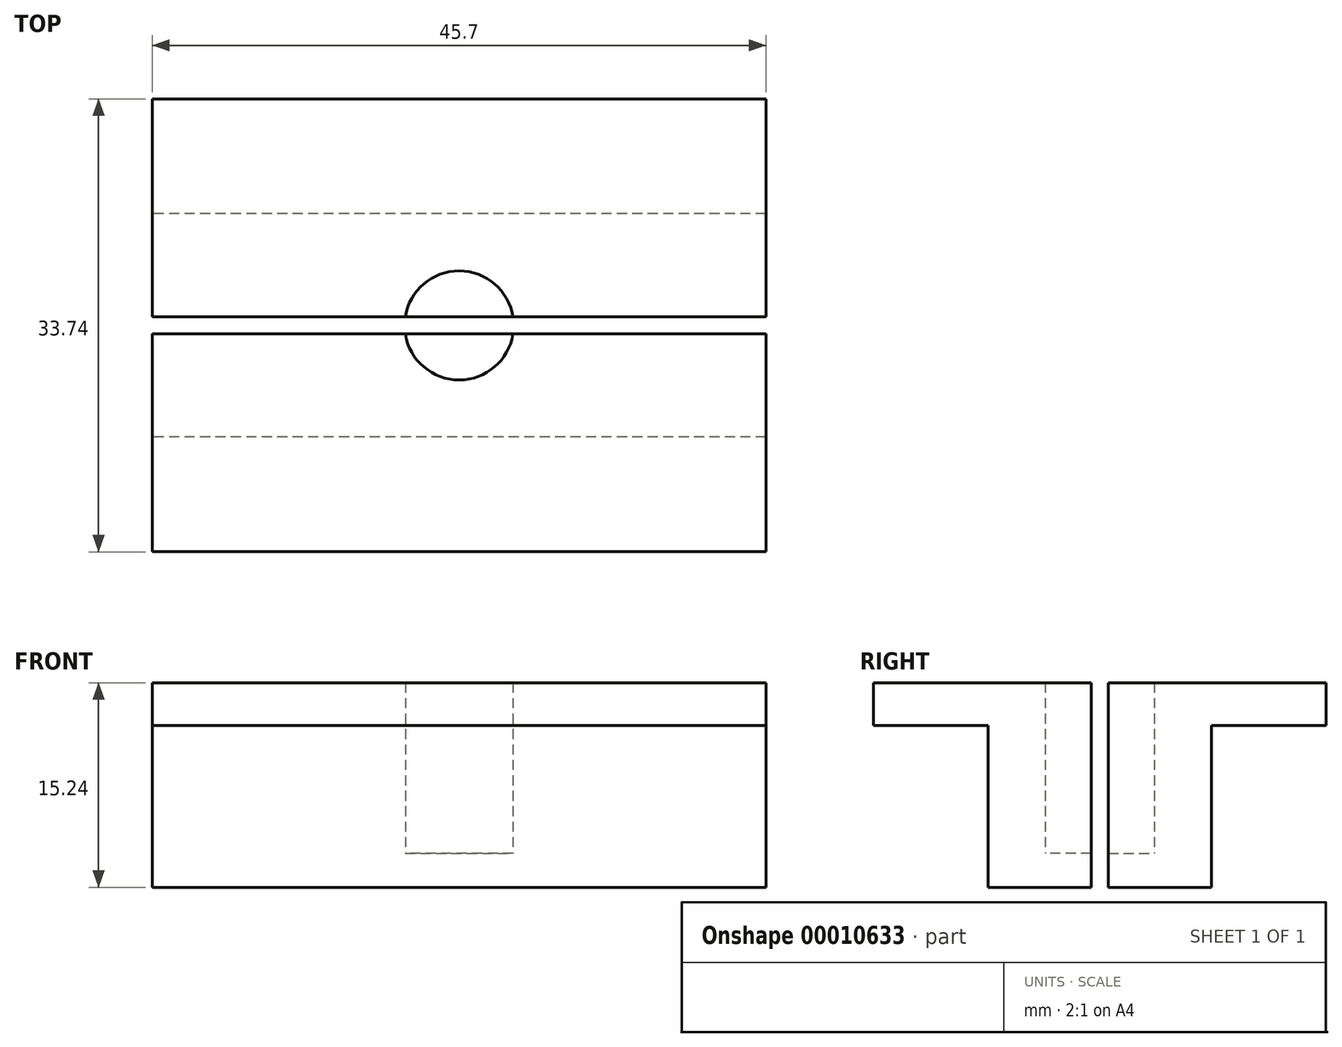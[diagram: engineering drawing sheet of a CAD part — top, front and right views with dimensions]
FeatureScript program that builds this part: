
annotation { "Feature Type Name" : "Feature", "Feature Type Description" : "" }
export const myFeature = defineFeature(function(context is Context, id is Id, definition is map)
    precondition{}
    {
        {
            var Q0;
            Q0=qCreatedBy(makeId("Top.planeOp"),FACE);
            var sketch = newSketch(context, id + "F0", { "sketchPlane" : qUnion([Q0])});
            skCircle(sketch, "E0", {"center": v(0, 0) * mm, "radius": 4.06 * mm});
            skLineSegment(sketch, "E1.rect.bottom", {"start": v(22.85, -8.3) * mm, "end": v(-22.85, -8.3) * mm});
            skLineSegment(sketch, "E1.rect.top", {"start": v(22.85, 8.3) * mm, "end": v(-22.85, 8.3) * mm});
            skLineSegment(sketch, "E1.rect.left", {"start": v(22.85, -8.3) * mm, "end": v(22.85, 8.3) * mm});
            skLineSegment(sketch, "E1.rect.right", {"start": v(-22.85, -8.3) * mm, "end": v(-22.85, 8.3) * mm});
            skSolve(sketch);
        }
        {
            var Q0;
            Q0=makeQuery(id+"F0.imprint","IMPRINT",FACE,{"disambiguationData":[TD([[makeQuery(id+"F0.imprint","IMPRINT",EDGE,{"derivedFrom":sQuery(id+"F0.wireOp",EDGE,"E0")}),-1.0]])]});
            extrude(context, id + "F1", {"entities" : qUnion([Q0]), "depth" : 12.7 * mm});
        }
        {
            var Q0;
            Q0=makeQuery(id+"F0.imprint","IMPRINT",FACE,{"disambiguationData":[TD([[makeQuery(id+"F0.imprint","IMPRINT",EDGE,{"derivedFrom":sQuery(id+"F0.wireOp",EDGE,"E0")}),1.0]])]});
            var Q1;
            Q1=makeQuery(id+"F0.imprint","IMPRINT",FACE,{"disambiguationData":[TD([[makeQuery(id+"F0.imprint","IMPRINT",EDGE,{"derivedFrom":sQuery(id+"F0.wireOp",EDGE,"E0")}),-1.0]])]});
            extrude(context, id + "F2", {"entities" : qUnion([Q0, Q1]), "operationType" : NewBodyOperationType.ADD, "oppositeDirection" : true, "depth" : 2.54 * mm});
        }
        {
            var Q0;
            Q0=makeQuery(id+"F1.opExtrude","CAP_FACE",FACE,{"disambiguationData":[OSD([sQuery(id+"F0.wireOp",EDGE,"E0"),sQuery(id+"F0.wireOp",EDGE,"E1.rect.bottom"),sQuery(id+"F0.wireOp",EDGE,"E1.rect.top"),sQuery(id+"F0.wireOp",EDGE,"E1.rect.left"),sQuery(id+"F0.wireOp",EDGE,"E1.rect.right")])],"isStart":false});
            var sketch = newSketch(context, id + "F3", { "sketchPlane" : qUnion([Q0])});
            skLineSegment(sketch, "E2", {"start": v(-34.06, 0) * mm, "end": v(37.41, 0) * mm, "construction": true});
            skLineSegment(sketch, "E3.bottom", {"start": v(-22.85, 8.3) * mm, "end": v(22.85, 8.3) * mm});
            skLineSegment(sketch, "E3.left", {"start": v(-22.85, 8.3) * mm, "end": v(-22.85, 16.87) * mm});
            skLineSegment(sketch, "E3.right", {"start": v(22.85, 8.3) * mm, "end": v(22.85, 16.87) * mm});
            skLineSegment(sketch, "E4.0.MirrorCS", {"start": v(22.85, -8.3) * mm, "end": v(22.85, -16.87) * mm});
            skLineSegment(sketch, "E5.0.MirrorCS", {"start": v(-22.85, -16.87) * mm, "end": v(-13.91, -16.87) * mm});
            skLineSegment(sketch, "E6.0.MirrorCS", {"start": v(-22.85, -8.3) * mm, "end": v(-22.85, -16.87) * mm});
            skLineSegment(sketch, "E7.0.MirrorCS", {"start": v(-22.85, -8.3) * mm, "end": v(22.85, -8.3) * mm});
            skLineSegment(sketch, "E8.trimOffspring", {"start": v(12.23, -16.87) * mm, "end": v(22.85, -16.87) * mm});
            skLineSegment(sketch, "E9.0.MirrorCS", {"start": v(-22.85, 16.87) * mm, "end": v(-13.91, 16.87) * mm});
            skLineSegment(sketch, "E10.0.MirrorCS", {"start": v(12.23, 16.87) * mm, "end": v(22.85, 16.87) * mm});
            skLineSegment(sketch, "E11", {"start": v(-13.91, 16.87) * mm, "end": v(12.23, 16.87) * mm});
            skLineSegment(sketch, "E12", {"start": v(-13.91, -16.87) * mm, "end": v(12.23, -16.87) * mm});
            skSolve(sketch);
        }
        {
            var Q0;
            Q0=makeQuery(id+"F3.imprint","IMPRINT",FACE,{"disambiguationData":[TD([[makeQuery(id+"F3.imprint","IMPRINT",EDGE,{"derivedFrom":sQuery(id+"F3.wireOp",EDGE,"E4.0.MirrorCS")}),-1.0]])]});
            var Q1;
            Q1=makeQuery(id+"F3.imprint","IMPRINT",FACE,{"disambiguationData":[TD([[makeQuery(id+"F3.imprint","IMPRINT",EDGE,{"derivedFrom":sQuery(id+"F3.wireOp",EDGE,"E3.bottom")}),-1.0]])]});
            extrude(context, id + "F4", {"entities" : qUnion([Q0, Q1]), "operationType" : NewBodyOperationType.ADD, "oppositeDirection" : true, "depth" : 3.18 * mm});
        }
        {
            var Q0;
            Q0=makeQuery(id+"F4.boolean.opBoolean","MERGE",FACE,{"derivedFrom":[makeQuery(id+"F1.opExtrude","CAP_FACE",FACE,{"disambiguationData":[OSD([sQuery(id+"F0.wireOp",EDGE,"E0"),sQuery(id+"F0.wireOp",EDGE,"E1.rect.bottom"),sQuery(id+"F0.wireOp",EDGE,"E1.rect.top"),sQuery(id+"F0.wireOp",EDGE,"E1.rect.left"),sQuery(id+"F0.wireOp",EDGE,"E1.rect.right")])],"isStart":false}),makeQuery(id+"F4.opExtrude","CAP_FACE",FACE,{"disambiguationData":[OSD([sQuery(id+"F3.wireOp",EDGE,"E3.bottom"),sQuery(id+"F3.wireOp",EDGE,"E3.left"),sQuery(id+"F3.wireOp",EDGE,"E3.right"),sQuery(id+"F3.wireOp",EDGE,"E9.0.MirrorCS"),sQuery(id+"F3.wireOp",EDGE,"cbe2b2d8-3755-455e-9f82-4391a709f186.0.MirrorCS"),sQuery(id+"F3.wireOp",EDGE,"E10.0.MirrorCS")])],"isStart":true}),makeQuery(id+"F4.opExtrude","CAP_FACE",FACE,{"disambiguationData":[OSD([sQuery(id+"F3.wireOp",EDGE,"E4.0.MirrorCS"),sQuery(id+"F3.wireOp",EDGE,"E5.0.MirrorCS"),sQuery(id+"F3.wireOp",EDGE,"E6.0.MirrorCS"),sQuery(id+"F3.wireOp",EDGE,"E7.0.MirrorCS"),sQuery(id+"F3.wireOp",EDGE,"b48b1b51-8ec0-4f0b-8ae0-5b7e94f44e96"),sQuery(id+"F3.wireOp",EDGE,"E8.trimOffspring")])],"isStart":true})]});
            var sketch = newSketch(context, id + "F5", { "sketchPlane" : qUnion([Q0])});
            skLineSegment(sketch, "E13.rect.bottom", {"start": v(26.28, -0.64) * mm, "end": v(-26.28, -0.64) * mm});
            skLineSegment(sketch, "E13.rect.top", {"start": v(26.28, 0.64) * mm, "end": v(-26.28, 0.64) * mm});
            skLineSegment(sketch, "E13.rect.left", {"start": v(26.28, -0.64) * mm, "end": v(26.28, 0.64) * mm});
            skLineSegment(sketch, "E13.rect.right", {"start": v(-26.28, -0.64) * mm, "end": v(-26.28, 0.64) * mm});
            skPoint(sketch, "E13.rect.middle", {"position": v(0, 0) * mm});
            skSolve(sketch);
        }
        {
            var Q0;
            {var subQ0=makeQuery(id+"F1.opExtrude","CAP_EDGE",EDGE,{"disambiguationData":[OSD([sQuery(id+"F0.wireOp",EDGE,"E0")])],"isStart":false});var subQ3=sQuery(id+"F5.wireOp",EDGE,"E13.rect.bottom");var subQ4=makeQuery(id+"F5.imprint","INTERSECT",VERTEX,{"disambiguationData":[OD(0.0)],"derivedFrom":[subQ0,subQ3]});Q0=makeQuery(id+"F5.imprint","IMPRINT",FACE,{"disambiguationData":[TD([[makeQuery(id+"F5.imprint","IMPRINT",EDGE,{"disambiguationData":[TD([[subQ4,-1.0]])],"derivedFrom":subQ0}),-1.0]])]});}
            var Q1;
            {var subQ0=makeQuery(id+"F1.opExtrude","CAP_EDGE",EDGE,{"disambiguationData":[OSD([sQuery(id+"F0.wireOp",EDGE,"E0")])],"isStart":false});var subQ3=sQuery(id+"F5.wireOp",EDGE,"E13.rect.bottom");var subQ6=makeQuery(id+"F5.imprint","INTERSECT",VERTEX,{"disambiguationData":[OD(0.0)],"derivedFrom":[subQ0,subQ3]});Q1=makeQuery(id+"F5.imprint","IMPRINT",FACE,{"disambiguationData":[TD([[makeQuery(id+"F5.imprint","IMPRINT",EDGE,{"disambiguationData":[TD([[subQ6,-1.0]])],"derivedFrom":subQ3}),-1.0]])]});}
            var Q2;
            {var subQ0=makeQuery(id+"F1.opExtrude","CAP_EDGE",EDGE,{"disambiguationData":[OSD([sQuery(id+"F0.wireOp",EDGE,"E0")])],"isStart":false});var subQ3=sQuery(id+"F5.wireOp",EDGE,"E13.rect.bottom");var subQ4=makeQuery(id+"F5.imprint","INTERSECT",VERTEX,{"disambiguationData":[OD(1.0)],"derivedFrom":[subQ0,subQ3]});Q2=makeQuery(id+"F5.imprint","IMPRINT",FACE,{"disambiguationData":[TD([[makeQuery(id+"F5.imprint","IMPRINT",EDGE,{"disambiguationData":[TD([[subQ4,1.0]])],"derivedFrom":subQ0}),-1.0]])]});}
            extrude(context, id + "F6", {"entities" : qUnion([Q0, Q1, Q2]), "operationType" : NewBodyOperationType.REMOVE, "endBound" : BoundingType.THROUGH_ALL, "oppositeDirection" : true, "depth" : 25.4 * mm});
        }
    });
